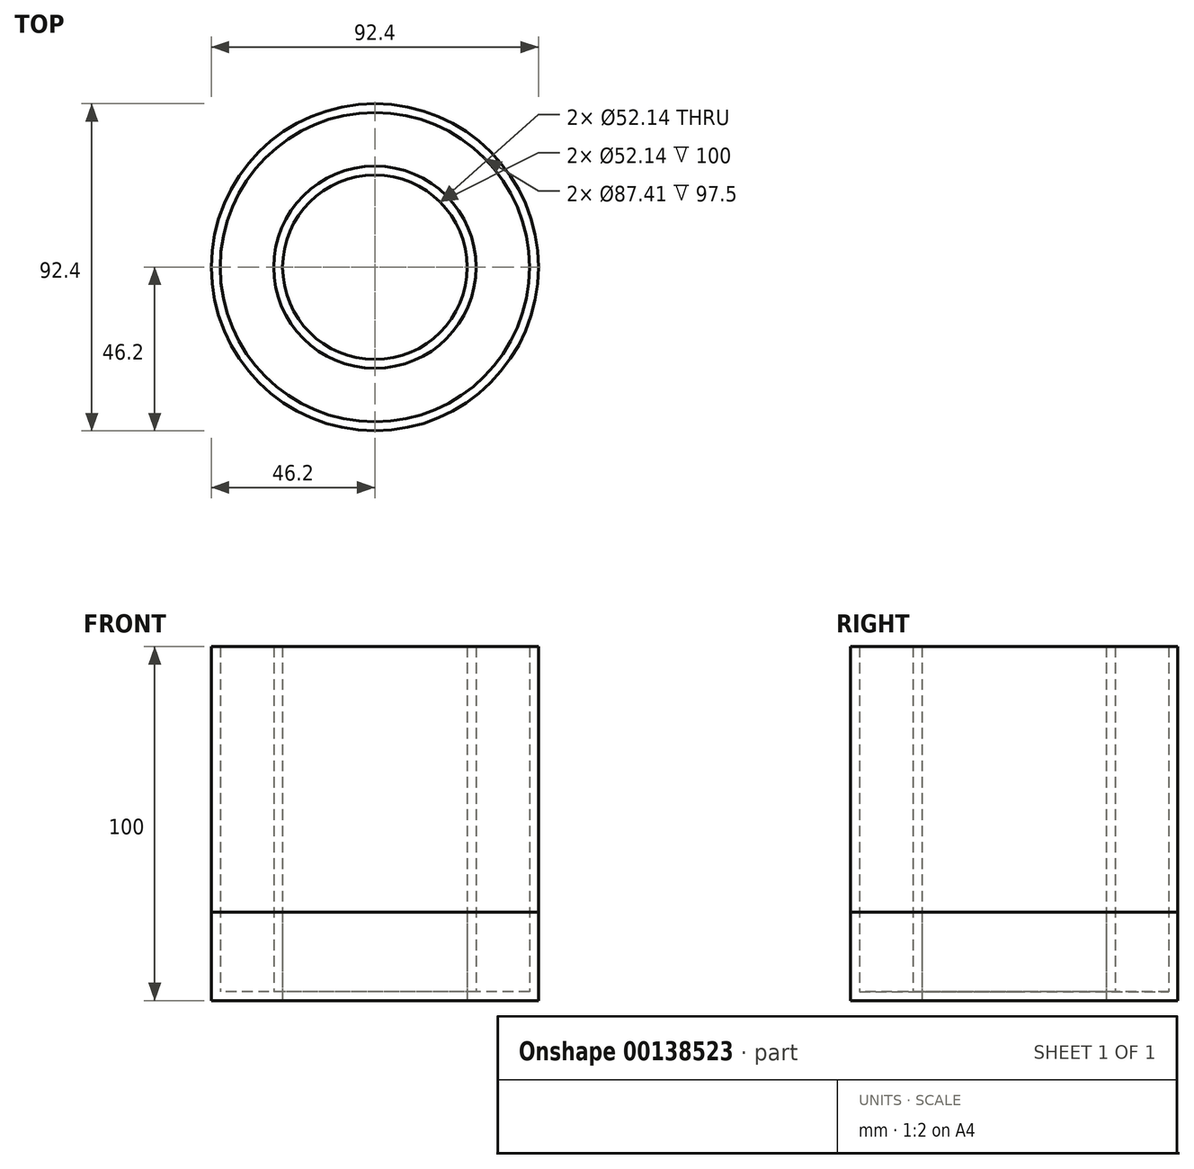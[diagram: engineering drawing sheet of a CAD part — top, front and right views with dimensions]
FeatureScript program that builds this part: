
annotation { "Feature Type Name" : "Feature", "Feature Type Description" : "" }
export const myFeature = defineFeature(function(context is Context, id is Id, definition is map)
    precondition{}
    {
        {
            var Q0;
            Q0=qCreatedBy(makeId("Top.planeOp"),FACE);
            var sketch = newSketch(context, id + "F0", { "sketchPlane" : qUnion([Q0])});
            skCircle(sketch, "E0", {"center": v(0, 0) * mm, "radius": 46.2 * mm});
            skCircle(sketch, "E1", {"center": v(0, 0) * mm, "radius": 26.07 * mm});
            skSolve(sketch);
        }
        {
            var Q0;
            Q0=makeQuery(id+"F0.imprint","IMPRINT",FACE,{"disambiguationData":[TD([[makeQuery(id+"F0.imprint","IMPRINT",EDGE,{"derivedFrom":sQuery(id+"F0.wireOp",EDGE,"E0")}),1.0]])]});
            extrude(context, id + "F1", {"entities" : qUnion([Q0]), "depth" : 25 * mm});
        }
        {
            var Q0;
            Q0 = qSketchRegion(id + "F0", true);
            extrude(context, id + "F2", {"entities" : qUnion([Q0]), "depth" : 100 * mm});
        }
        {
            var Q0;
            Q0=makeQuery(id+"F2.opExtrude","CAP_FACE",FACE,{"disambiguationData":[OSD([sQuery(id+"F0.wireOp",EDGE,"E0"),sQuery(id+"F0.wireOp",EDGE,"E1")])],"isStart":false});
            shell(context, id + "F3", {"entities" : qUnion([Q0]), "thickness" : 2.5 * mm});
        }
    });
